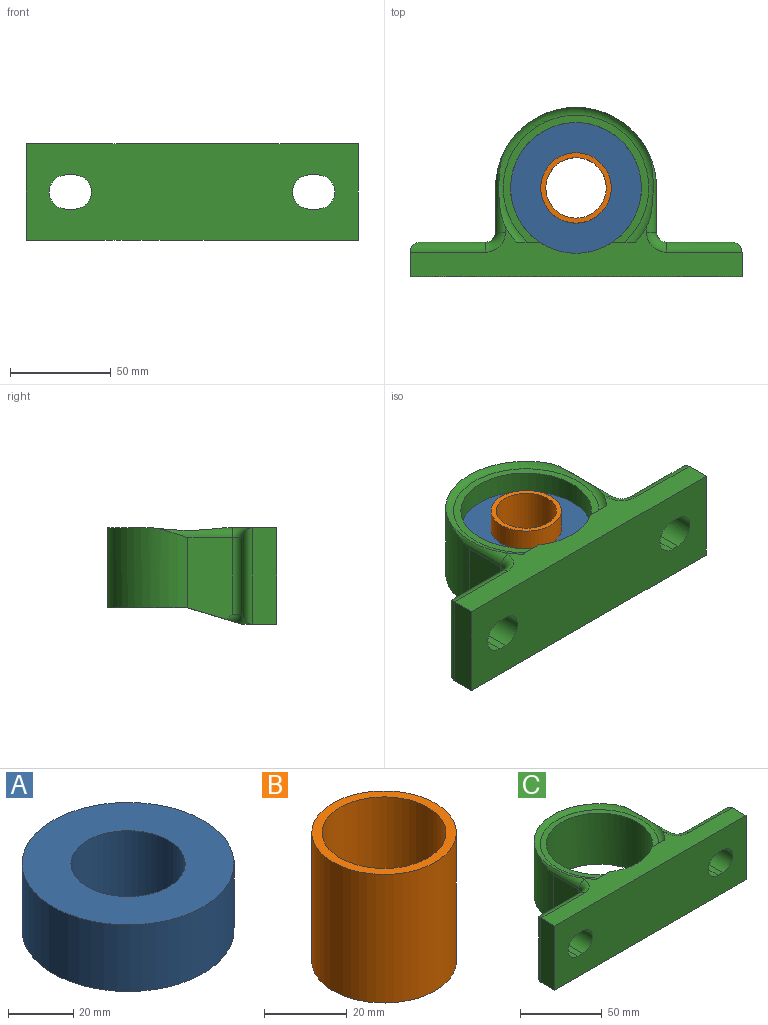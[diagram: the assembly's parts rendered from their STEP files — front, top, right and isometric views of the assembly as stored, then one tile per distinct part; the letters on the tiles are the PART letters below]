
ASSEMBLY  parts=3 mates=2
PART A: 4 faces, bbox 65x65x25 mm
  f0: cylinder r=17.5mm len=35mm, axis (0,0,-1), area 2748.9mm2, adj f2,f3
  f1: cylinder r=32.5mm len=65mm, axis (0,0,-1), area 5105.1mm2, adj f2,f3
  f2: plane 65x65mm, normal (0,0,1), area 2356.2mm2, adj f0,f1
  f3: plane 65x65mm, normal (0,0,-1), area 2356.2mm2, adj f0,f1
PART B: 4 faces, bbox 35x35x38.1 mm
  f0: cylinder r=15mm len=38.1mm, axis (0,0,-1), area 3590.8mm2, adj f2,f3
  f1: cylinder r=17.5mm len=38.1mm, axis (0,0,-1), area 4189.3mm2, adj f2,f3
  f2: plane 35x35mm, normal (0,0,1), area 255.3mm2, adj f0,f1
  f3: plane 35x35mm, normal (0,0,-1), area 255.3mm2, adj f0,f1
PART C: 48 faces, bbox 165.2x88.7x51.4 mm
  f0: plane 165x48mm, normal (0,-1,0), area 7330mm2, adj f6,f9,f14,f15,f40,f41,f42,f43
  f1: plane 38x32.5mm, normal (0,1,0), area 940mm2, adj f27,f29,f30,f31,f44,f45,f46,f47
  f2: plane 40.77x22.13mm, normal (1,0,0), area 835.6mm2, adj f16,f20,f27,f28,f33
  f3: plane 40.77x22.13mm, normal (-1,0,0), area 835.6mm2, adj f16,f19,f26,f34,f39
  f4: cylinder r=40mm len=10.33mm, axis (0,0,-1), area 19.3mm2, adj f7,f20,f25
  f5: cylinder r=40mm len=10.33mm, axis (0,0,-1), area 19.3mm2, adj f8,f19,f23
  f6: plane 165x17mm, normal (0,0,-1), area 2233.5mm2, adj f0,f7,f8,f9,f11,f14,f19,f20
  f7: plane 11.42x3.1mm, normal (0,1,0), area 35.4mm2, adj f4,f6,f11,f24
  f8: plane 11.42x3.1mm, normal (0,1,0), area 35.4mm2, adj f5,f6,f11,f22
  f9: plane 48x12mm, normal (1,0,0), area 576mm2, adj f0,f6,f15,f30
  f10: plane 11.42x1.8mm, normal (0,1,0), area 17.6mm2, adj f11,f15,f17,f21
  f11: cylinder r=32.5mm len=65mm, axis (0,0,-1), area 8177.9mm2, adj f6,f7,f8,f10,f12,f15,f17,f18
  f12: plane 11.42x1.8mm, normal (0,1,0), area 17.6mm2, adj f11,f15,f17,f21
  f13: plane 38x32.5mm, normal (0,1,0), area 940mm2, adj f26,f35,f36,f37,f40,f41,f42,f43
  f14: plane 48x12mm, normal (-1,0,0), area 576mm2, adj f0,f6,f15,f36
  f15: plane 165x24.64mm, normal (0,0,1), area 2276.3mm2, adj f0,f9,f10,f11,f12,f14,f21,f31
  f16: cylinder r=40mm len=80mm, axis (0,0,-1), area 4935.6mm2, adj f2,f3,f18,f21,f33,f39
  f17: plane 72.32x63.16mm, normal (0,0,1), area 622.1mm2, adj f10,f11,f12,f21
  f18: plane 80x62mm, normal (0,0,-1), area 974mm2, adj f11,f16,f19,f20,f22,f23,f24,f25
  f19: plane 27.16x10.65mm, normal (0,0.29,-0.96), area 98.6mm2, adj f3,f5,f6,f18,f23,f34
  f20: plane 27.16x10.65mm, normal (0,0.29,-0.96), area 98.6mm2, adj f2,f4,f6,f18,f25,f28
  f21: torus R=36.16mm, axis (0,0,-1), area 694.9mm2, adj f10,f12,f15,f16,f17,f33,f39
  f22: cylinder r=5mm len=11.42mm, axis (1,0,0), area 65.1mm2, adj f8,f11,f18,f23
  f23: torus R=35mm, axis (0,0,1), area 167.8mm2, adj f5,f18,f19,f22
  f24: cylinder r=5mm len=11.42mm, axis (1,0,0), area 65.1mm2, adj f7,f11,f18,f25
  f25: torus R=35mm, axis (0,0,1), area 167.8mm2, adj f4,f18,f20,f24
  f26: cylinder r=5mm len=38mm, axis (0,0,-1), area 298.5mm2, adj f3,f13,f34,f38
  f27: cylinder r=5mm len=38mm, axis (0,0,-1), area 298.5mm2, adj f1,f2,f28,f32
  f28: torus R=10mm, axis (0,0,1), area 75.9mm2, adj f2,f6,f20,f27,f29
  f29: cylinder r=5mm len=37.5mm, axis (-1,0,0), area 280.3mm2, adj f1,f6,f28,f30
  f30: cylinder r=5mm len=48mm, axis (0,0,-1), area 348.5mm2, adj f1,f9,f29,f31
  f31: cylinder r=5mm len=37.5mm, axis (1,0,0), area 280.3mm2, adj f1,f15,f30,f32
  f32: torus R=10mm, axis (0,0,1), area 84.1mm2, adj f15,f27,f31,f33
  f33: cylinder r=5mm len=41.37mm, axis (0,-1,0), area 152.2mm2, adj f2,f15,f16,f21,f32
  f34: torus R=10mm, axis (0,0,1), area 75.9mm2, adj f3,f6,f19,f26,f35
  f35: cylinder r=5mm len=37.5mm, axis (-1,0,0), area 280.3mm2, adj f6,f13,f34,f36
  f36: cylinder r=5mm len=48mm, axis (0,0,-1), area 348.5mm2, adj f13,f14,f35,f37
  f37: cylinder r=5mm len=37.5mm, axis (1,0,0), area 280.3mm2, adj f13,f15,f36,f38
  f38: torus R=10mm, axis (0,0,1), area 84.1mm2, adj f15,f26,f37,f39
  f39: cylinder r=5mm len=41.37mm, axis (0,1,0), area 152.2mm2, adj f3,f15,f16,f21,f38
  f40: cylinder r=8.5mm len=17mm, axis (0,1,0), area 454mm2, adj f0,f13,f41,f43
  f41: plane 17x4mm, normal (0,0,1), area 68mm2, adj f0,f13,f40,f42
  f42: cylinder r=8.5mm len=17mm, axis (0,1,0), area 454mm2, adj f0,f13,f41,f43
  f43: plane 17x4mm, normal (0,0,-1), area 68mm2, adj f0,f13,f40,f42
  f44: cylinder r=8.5mm len=17mm, axis (0,1,0), area 454mm2, adj f0,f1,f45,f47
  f45: plane 17x4mm, normal (0,0,1), area 68mm2, adj f0,f1,f44,f46
  f46: cylinder r=8.5mm len=17mm, axis (0,1,0), area 454mm2, adj f0,f1,f45,f47
  f47: plane 17x4mm, normal (0,0,-1), area 68mm2, adj f0,f1,f44,f46
PLACE A t=(-61.43,76.62,81.72)mm
PLACE B t=(-61.43,76.62,81.72)mm
PLACE C t=(-61.43,76.62,81.72)mm
MATE fastened C.f11 <-> B.f1  axis (0,0,-1) through (-61.43,76.62,89.82)mm
MATE fastened B.f1 <-> A.f1  axis (0,0,-1) through (-61.43,76.62,89.82)mm
